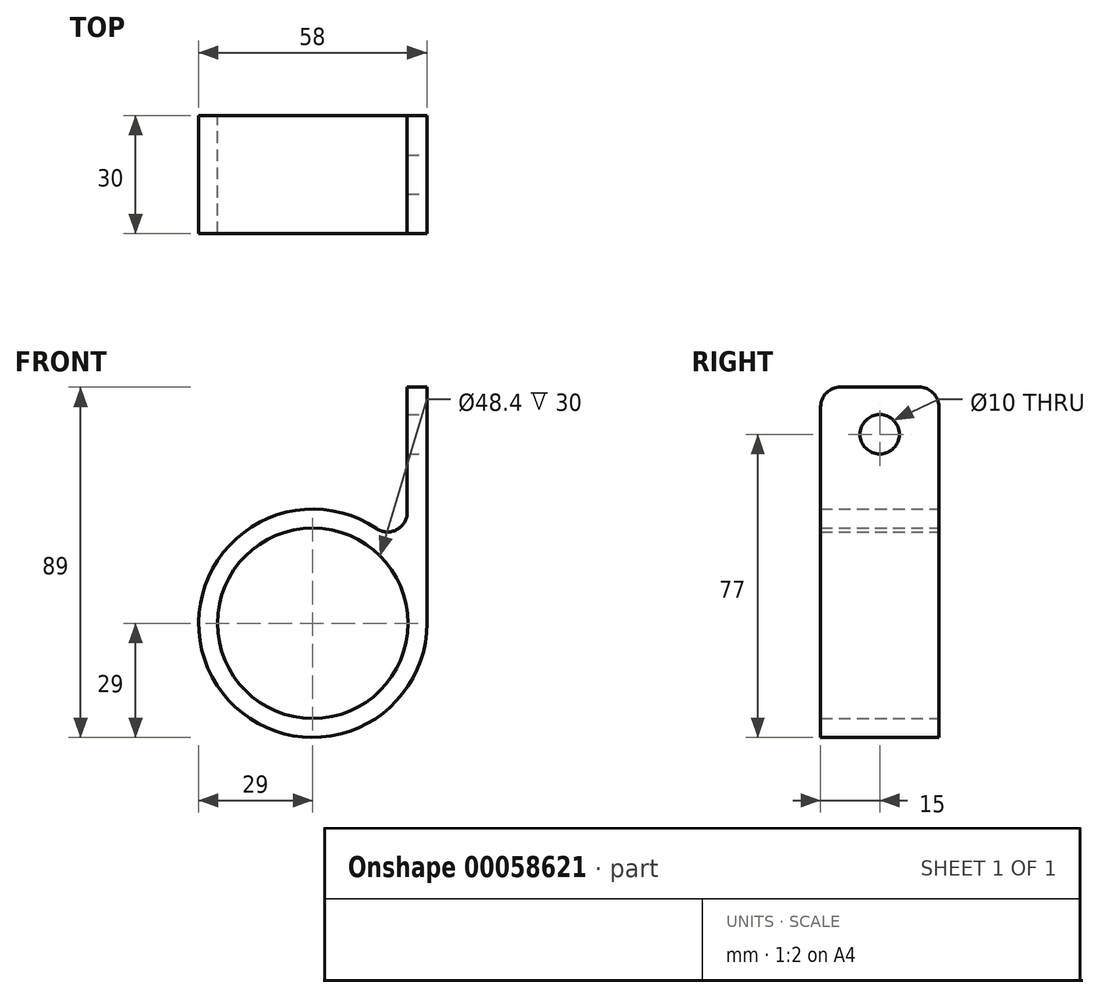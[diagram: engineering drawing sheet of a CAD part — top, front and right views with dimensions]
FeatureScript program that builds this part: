
annotation { "Feature Type Name" : "Feature", "Feature Type Description" : "" }
export const myFeature = defineFeature(function(context is Context, id is Id, definition is map)
    precondition{}
    {
        {
            var Q0;
            Q0=qCreatedBy(makeId("Front.planeOp"),FACE);
            var sketch = newSketch(context, id + "F0", { "sketchPlane" : qUnion([Q0])});
            skCircle(sketch, "E0", {"center": v(0, 0) * mm, "radius": 24.2 * mm});
            skArc(sketch, "E1", {"start": v(24, 16.28) * mm, "mid": v(-27.72, -8.51) * mm, "end": v(29, 0) * mm});
            skLineSegment(sketch, "E2", {"start": v(29, 0) * mm, "end": v(29, 60) * mm});
            skLineSegment(sketch, "E3", {"start": v(29, 60) * mm, "end": v(24, 60) * mm});
            skLineSegment(sketch, "E4", {"start": v(24, 60) * mm, "end": v(24, 16.28) * mm});
            skSolve(sketch);
        }
        {
            var Q0;
            Q0 = qSketchRegion(id + "F0", true);
            extrude(context, id + "F1", {"entities" : qUnion([Q0]), "depth" : 30 * mm});
        }
        {
            var Q0;
            Q0=makeQuery(id+"F1.opExtrude","SWEPT_FACE",FACE,{"disambiguationData":[OSD([sQuery(id+"F0.wireOp",EDGE,"E2")])]});
            var sketch = newSketch(context, id + "F2", { "sketchPlane" : qUnion([Q0])});
            skCircle(sketch, "E5", {"center": v(-15, 48) * mm, "radius": 5 * mm});
            skPoint(sketch, "E5.centerSnap0", {"position": v(-15, 60) * mm});
            skSolve(sketch);
        }
        {
            var Q0;
            Q0 = qSketchRegion(id + "F2", true);
            extrude(context, id + "F3", {"entities" : qUnion([Q0]), "operationType" : NewBodyOperationType.REMOVE, "oppositeDirection" : true, "depth" : 25 * mm});
        }
        {
            var Q0;
            Q0=makeQuery(id+"F1.opExtrude","SWEPT_EDGE",EDGE,{"disambiguationData":[OSD([sQuery(id+"F0.wireOp",EDGE,"E1"),sQuery(id+"F0.wireOp",EDGE,"E4")])]});
            var Q1;
            Q1=makeQuery(id+"F1.opExtrude","CAP_EDGE",EDGE,{"disambiguationData":[OSD([sQuery(id+"F0.wireOp",EDGE,"E3")])],"isStart":false});
            var Q2;
            Q2=makeQuery(id+"F1.opExtrude","CAP_EDGE",EDGE,{"disambiguationData":[OSD([sQuery(id+"F0.wireOp",EDGE,"E3")])],"isStart":true});
            fillet(context, id + "F4", {"entities" : qUnion([Q0, Q1, Q2]), "radius" : 5 * mm, "tangentPropagation" : true, "allowEdgeOverflow" : false});
        }
    });
